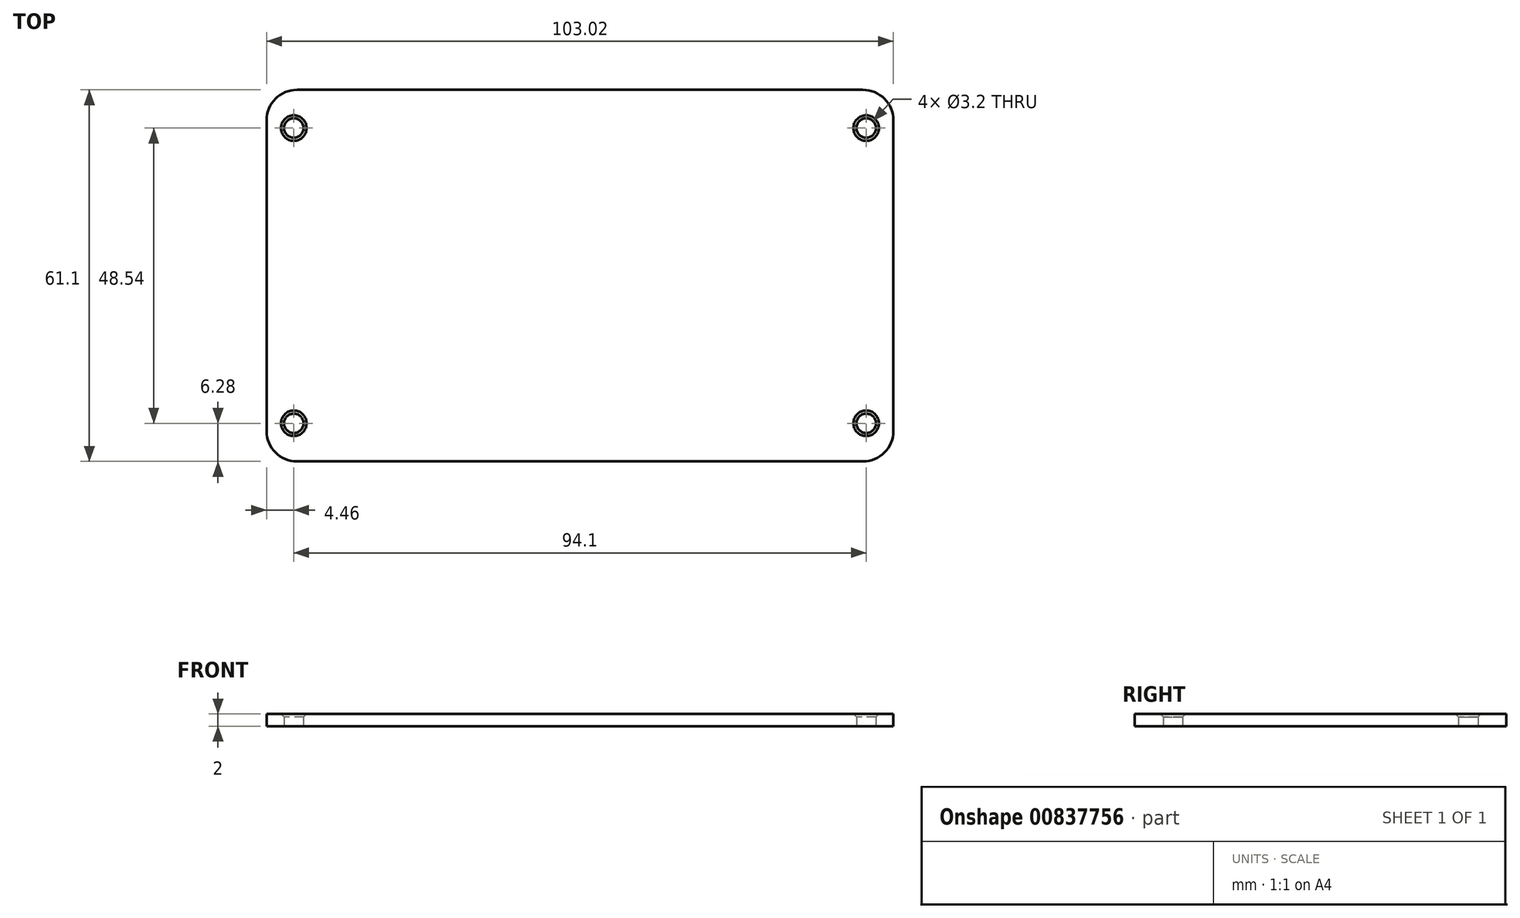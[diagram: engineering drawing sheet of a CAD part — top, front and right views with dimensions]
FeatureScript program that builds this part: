
annotation { "Feature Type Name" : "Feature", "Feature Type Description" : "" }
export const myFeature = defineFeature(function(context is Context, id is Id, definition is map)
    precondition{}
    {
        {
            var Q0;
            Q0=qCreatedBy(makeId("Top.planeOp"),FACE);
            var sketch = newSketch(context, id + "F0", { "sketchPlane" : qUnion([Q0])});
            skLineSegment(sketch, "E0.bottom", {"start": v(45.45, -24.27) * mm, "end": v(42.8, -24.27) * mm});
            skCircle(sketch, "E1", {"center": v(47.05, 24.27) * mm, "radius": 1.6 * mm});
            skCircle(sketch, "E2", {"center": v(47.05, -24.27) * mm, "radius": 1.6 * mm});
            skCircle(sketch, "E3", {"center": v(-47.05, 24.27) * mm, "radius": 1.6 * mm});
            skCircle(sketch, "E4", {"center": v(-47.05, -24.27) * mm, "radius": 1.6 * mm});
            skLineSegment(sketch, "E5.bottom", {"start": v(51.51, 30.55) * mm, "end": v(-51.51, 30.55) * mm});
            skLineSegment(sketch, "E5.top", {"start": v(51.51, -30.55) * mm, "end": v(-51.51, -30.55) * mm});
            skLineSegment(sketch, "E5.left", {"start": v(51.51, 30.55) * mm, "end": v(51.51, -30.55) * mm});
            skLineSegment(sketch, "E5.right", {"start": v(-51.51, 30.55) * mm, "end": v(-51.51, -30.55) * mm});
            skPoint(sketch, "E6.end.orphan", {"position": v(0, 30.55) * mm});
            skPoint(sketch, "E6.start.orphan", {"position": v(0, 27.55) * mm});
            skLineSegment(sketch, "E7.bottom", {"start": v(51.51, 30.55) * mm, "end": v(91.51, 30.55) * mm});
            skLineSegment(sketch, "E7.top", {"start": v(51.51, -30.55) * mm, "end": v(91.51, -30.55) * mm});
            skLineSegment(sketch, "E7.right", {"start": v(91.51, 30.55) * mm, "end": v(91.51, -30.55) * mm});
            skSolve(sketch);
        }
        {
            var Q0;
            Q0=makeQuery(id+"F0.imprint","IMPRINT",FACE,{"disambiguationData":[TD([[makeQuery(id+"F0.imprint","IMPRINT",EDGE,{"derivedFrom":sQuery(id+"F0.wireOp",EDGE,"E1")}),-1.0]])]});
            extrude(context, id + "F1", {"entities" : qUnion([Q0]), "depth" : 2 * mm, "offsetDistance" : 25 * mm});
        }
        {
            var Q0;
            Q0=makeQuery(id+"F1.opExtrude","SWEPT_EDGE",EDGE,{"disambiguationData":[OSD([sQuery(id+"F0.wireOp",EDGE,"E5.top"),sQuery(id+"F0.wireOp",EDGE,"E5.right")])]});
            var Q1;
            Q1=makeQuery(id+"F1.opExtrude","SWEPT_EDGE",EDGE,{"disambiguationData":[OSD([sQuery(id+"F0.wireOp",EDGE,"E5.bottom"),sQuery(id+"F0.wireOp",EDGE,"E5.right")])]});
            var Q2;
            Q2=makeQuery(id+"F1.opExtrude","SWEPT_EDGE",EDGE,{"disambiguationData":[OSD([sQuery(id+"F0.wireOp",EDGE,"E5.top"),sQuery(id+"F0.wireOp",EDGE,"E5.left")])]});
            var Q3;
            Q3=makeQuery(id+"F1.opExtrude","SWEPT_EDGE",EDGE,{"disambiguationData":[OSD([sQuery(id+"F0.wireOp",EDGE,"E5.bottom"),sQuery(id+"F0.wireOp",EDGE,"E5.left")])]});
            fillet(context, id + "F2", {"entities" : qUnion([Q0, Q1, Q2, Q3]), "radius" : 5 * mm, "tangentPropagation" : true, "allowEdgeOverflow" : false});
        }
        {
            var Q0;
            Q0=makeQuery(id+"F1.opExtrude","CAP_EDGE",EDGE,{"disambiguationData":[OSD([sQuery(id+"F0.wireOp",EDGE,"E4")])],"isStart":false});
            var Q1;
            Q1=makeQuery(id+"F1.opExtrude","CAP_EDGE",EDGE,{"disambiguationData":[OSD([sQuery(id+"F0.wireOp",EDGE,"E3")])],"isStart":false});
            var Q2;
            Q2=makeQuery(id+"F1.opExtrude","CAP_EDGE",EDGE,{"disambiguationData":[OSD([sQuery(id+"F0.wireOp",EDGE,"E1")])],"isStart":false});
            var Q3;
            Q3=makeQuery(id+"F1.opExtrude","CAP_EDGE",EDGE,{"disambiguationData":[OSD([sQuery(id+"F0.wireOp",EDGE,"E2")])],"isStart":false});
            chamfer(context, id + "F3", {"entities" : qUnion([Q0, Q1, Q2, Q3]), "width" : 0.5 * mm, "tangentPropagation" : true});
        }
    });
